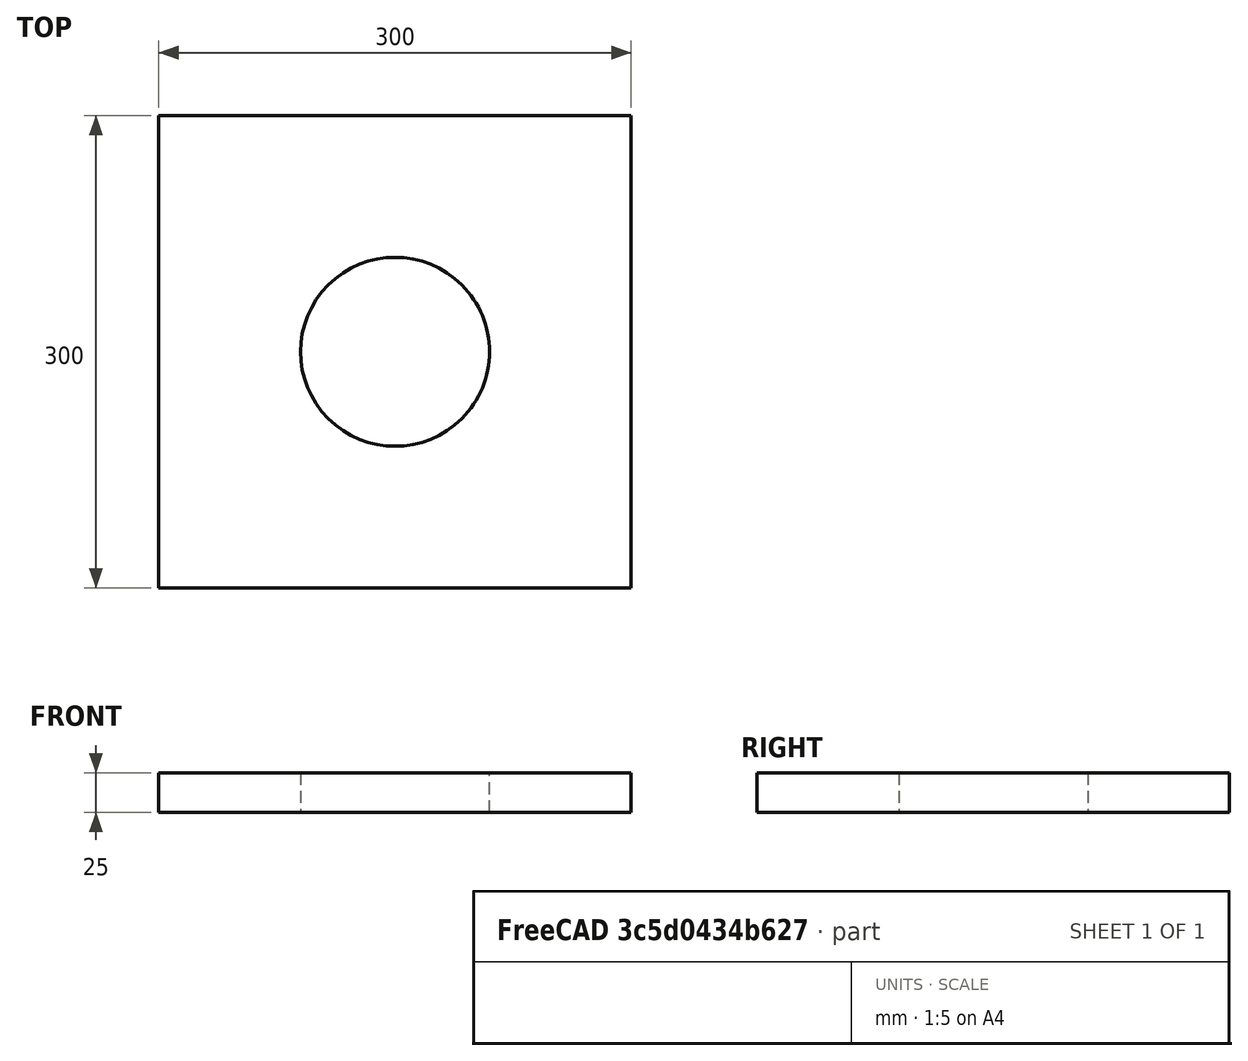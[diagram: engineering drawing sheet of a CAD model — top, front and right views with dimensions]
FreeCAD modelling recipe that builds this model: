
FCSTD DOCUMENT  (FreeCAD 0.21R33694 (Git))
Label: Lug_Pressure_Example
License: All rights reserved
LicenseURL: http://en.wikipedia.org/wiki/All_rights_reserved
objects: Part::FeaturePython×5, Sketcher::SketchObject×2, Part::Extrusion×2, Fem::FemSolverObjectPython×1, Fem::ConstraintFixed×1, Part::MultiFuse×1, Fem::ConstraintPressure×1, App::MaterialObjectPython×1, Fem::FemMeshObjectPython×1, Fem::FemAnalysis×1
note: 10 computed .brp shape members not serialized (recipe doc carries the construction recipe); baked Part::Feature solids carry a one-line shape summary decoded from their .brp

FEATURE [Sketcher::SketchObject] Sketch
  FullyConstrained = true
  Placement = pos=(150,0,0) rot=(0,0,1;0rad)
  sketch-geometry (5):
    g0: LineSegment StartX=0 StartY=0 StartZ=0 EndX=300 EndY=0 EndZ=0
    g1: LineSegment StartX=300 StartY=0 StartZ=0 EndX=300 EndY=300 EndZ=0
    g2: LineSegment StartX=300 StartY=300 StartZ=0 EndX=0 EndY=300 EndZ=0
    g3: LineSegment StartX=0 StartY=300 StartZ=0 EndX=0 EndY=0 EndZ=0
    g4: Circle CenterX=150 CenterY=150 CenterZ=0 NormalX=0 NormalY=0 NormalZ=1 AngleXU=0 Radius=60
  constraints (14):
    c: Coincident(g0,g1)
    c: Coincident(g1,g2)
    c: Coincident(g2,g3)
    c: Coincident(g3,g0)
    c: Horizontal(g0)
    c: Horizontal(g2)
    c: Vertical(g1)
    c: Vertical(g3)
    c: Coincident(g0,g-1)
    c: DistanceY(g1,g1) = 300
    c: DistanceX(g0,g0) = 300
    c: DistanceX(g0,g4) = 150
    c: DistanceY(g0,g4) = 150
    c: Radius(g4) = 60
FEATURE [Part::Extrusion] Extrude
  Base = -> Sketch
  Dir = (0,0,1)
  DirMode = 2
  FaceMakerClass = Part::FaceMakerBullseye
  LengthFwd = 25
  LengthRev = 0
  Solid = true
  Symmetric = false
FEATURE [Fem::FemSolverObjectPython] SolverCcxTools  # FEM object (typed FeaturePython)
  AnalysisType = 0
  BeamShellResultOutput3D = false
  BucklingFactors = 1
  EigenmodeHighLimit = 1000000
  EigenmodeLowLimit = 0
  EigenmodesCount = 10
  GeometricalNonlinearity = 0
  IterationsControlParameterCutb = 0.25,0.5,0.75,0.85,,,1.5,
  IterationsControlParameterIter = 4,8,9,200,10,400,,200,,
  IterationsControlParameterTimeUse = false
  IterationsThermoMechMaximum = 200
  IterationsUserDefinedIncrementations = false
  IterationsUserDefinedTimeStepLength = false
  MaterialNonlinearity = 0
  MatrixSolverType = 0
  SplitInputWriter = false
  ThermoMechSteadyState = true
  TimeEnd = 1
  TimeInitialStep = 1
FEATURE [Fem::ConstraintFixed] ConstraintFixed001
  NormalDirection = (0,-1,0)
  Normals = (16) [(0,-1,0),(0,-1,0),(0,-1,0),(0,-1,0),(0,-1,0),(0,-1,0),(0,-1,0),(0,-1,0),(0,-1,0),(0,-1,0),(0,-1,0),(0,-1,0),(0,-1,0),(0,-1,0),(0,-1,0),(0,-1,0)]
  Points = (16) [(150,0,25),(250,0,25),(350,0,25),(450,0,25),(150,0,16.6667),(250,0,16.6667),(350,0,16.6667),(450,0,16.6667),(150,0,8.33333),(250,0,8.33333),+6 more]
  References = -> [Extrude]
  Scale = 13
FEATURE [Sketcher::SketchObject] Sketch001
  FullyConstrained = true
  sketch-geometry (2):
    g0: LineSegment StartX=150 StartY=300 StartZ=0 EndX=450 EndY=0 EndZ=0
    g1: LineSegment StartX=150 StartY=0 StartZ=0 EndX=450 EndY=300 EndZ=0
  constraints (8):
    c: DistanceX(g1) = 150
    c: DistanceY(g1,g-1) = 0
    c: DistanceY(g0,g-1) = 0
    c: DistanceX(g1,g0) = 300
    c: DistanceX(g-1,g0) = 150
    c: DistanceX(g-1,g1) = 450
    c: DistanceY(g-1,g0) = 300
    c: DistanceY(g-1,g1) = 300
FEATURE [Part::Extrusion] Extrude001
  Base = -> Sketch001
  Dir = (0,0,1)
  DirMode = 0
  FaceMakerClass = Part::FaceMakerBullseye
  LengthFwd = 25
  LengthRev = 0
  Solid = false
  Symmetric = false
FEATURE [Part::FeaturePython] Slice  # WARN: FeaturePython — macro-defined, semantics opaque (R4)
  Base = -> Extrude
  Mode = 1
  Tolerance = 0
  Tools = -> [Extrude001]
FEATURE [Part::FeaturePython] Slice_child0  label="Slice.0"  # WARN: FeaturePython — macro-defined, semantics opaque (R4)
  Base = -> Slice
  FilterType = 1
  Invert = false
  OverrideMaxVal = 0
  WindowFrom = 80
  WindowTo = 100
  items = 0
FEATURE [Part::FeaturePython] Slice_child1  label="Slice.1"  # WARN: FeaturePython — macro-defined, semantics opaque (R4)
  Base = -> Slice
  FilterType = 1
  Invert = false
  OverrideMaxVal = 0
  WindowFrom = 80
  WindowTo = 100
  items = 1
FEATURE [Part::FeaturePython] Slice_child2  label="Slice.2"  # WARN: FeaturePython — macro-defined, semantics opaque (R4)
  Base = -> Slice
  FilterType = 1
  Invert = false
  OverrideMaxVal = 0
  WindowFrom = 80
  WindowTo = 100
  items = 2
FEATURE [Part::FeaturePython] Slice_child3  label="Slice.3"  # WARN: FeaturePython — macro-defined, semantics opaque (R4)
  Base = -> Slice
  FilterType = 1
  Invert = false
  OverrideMaxVal = 0
  WindowFrom = 80
  WindowTo = 100
  items = 3
FEATURE [Part::MultiFuse] Fusion001  label="Fusion_25mm"
  Shapes = -> [Slice_child0,Slice_child1,Slice_child2,Slice_child3]
FEATURE [Fem::ConstraintPressure] ConstraintPressure
  NormalDirection = (-0.92388,-0.382683,0)
  Normals = (32) [(-1,0,0),(-0.965926,-0.258819,0),(-0.866025,-0.5,0),(-0.707107,-0.707107,0),(-1,0,0),(-0.965926,-0.258819,0),(-0.866025,-0.5,0),+25 more]
  Points = (32) [(360,150,25),(357.956,165.529,25),(351.962,180,25),(342.426,192.426,25),(360,150,16.6667),(357.956,165.529,16.6667),(351.962,180,16.6667),+25 more]
  Pressure = 100
  References = -> [Fusion001]
  Scale = 5
FEATURE [App::MaterialObjectPython] MaterialSolid  # material (typed FeaturePython)
  Category = 0
  Material = AuthorAndLicense=(c) 2014 M. Münch - GNU Lesser General Public License (LGPL),CardName=Steel-St-E-315,Density=7800 kg/m^3,Father=Metal,+13 more (map truncated)
FEATURE [Fem::FemMeshObjectPython] FEMMeshGmsh  # FEM object (typed FeaturePython)
  Algorithm2D = 0
  Algorithm3D = 0
  CharacteristicLengthMax = 0
  CharacteristicLengthMin = 0
  CoherenceMesh = true
  ElementDimension = 0
  ElementOrder = 1
  GeometryTolerance = 1e-06
  GroupsOfNodes = false
  HighOrderOptimize = 0
  MeshSizeFromCurvature = 12
  OptimizeNetgen = false
  OptimizeStd = true
  Part = -> Fusion001
  RecombinationAlgorithm = 0
  Recombine3DAll = false
  RecombineAll = false
  SecondOrderLinear = false
FEATURE [Fem::FemAnalysis] Analysis
  Group = -> [SolverCcxTools,MaterialSolid,ConstraintFixed001,ConstraintPressure,FEMMeshGmsh]
